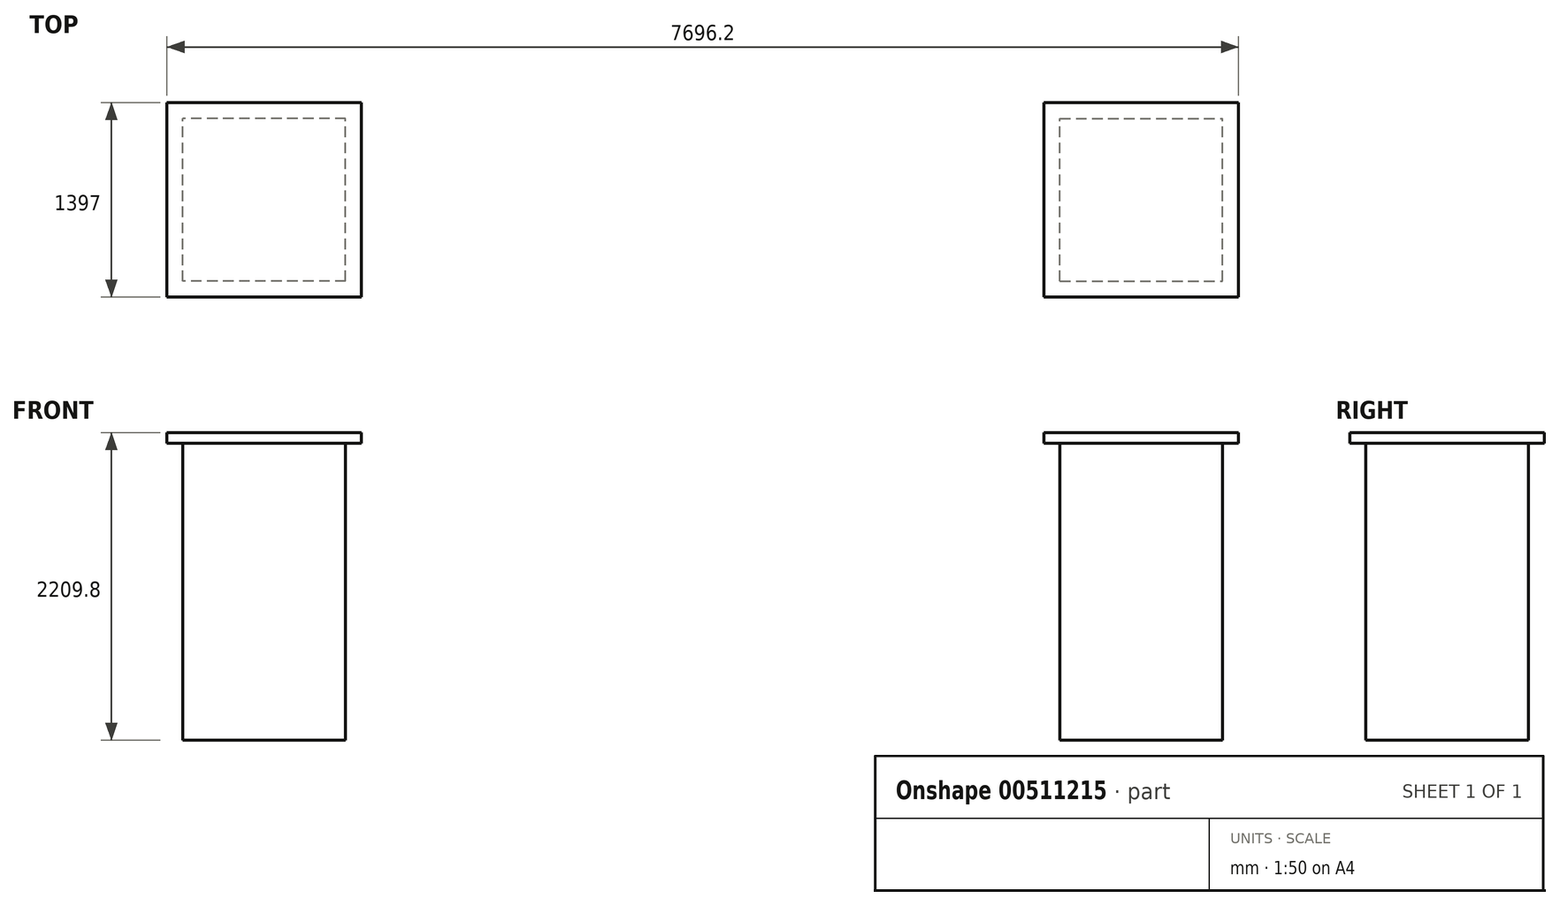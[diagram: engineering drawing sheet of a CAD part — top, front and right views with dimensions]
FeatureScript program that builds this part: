
annotation { "Feature Type Name" : "Feature", "Feature Type Description" : "" }
export const myFeature = defineFeature(function(context is Context, id is Id, definition is map)
    precondition{}
    {
        {
            var Q0;
            Q0=qCreatedBy(makeId("Top.planeOp"),FACE);
            var sketch = newSketch(context, id + "F0", { "sketchPlane" : qUnion([Q0])});
            skLineSegment(sketch, "E0.bottom", {"start": v(-2565.4, -584.2) * mm, "end": v(-3733.8, -584.2) * mm});
            skLineSegment(sketch, "E0.top", {"start": v(-2565.4, 584.2) * mm, "end": v(-3733.8, 584.2) * mm});
            skLineSegment(sketch, "E0.left", {"start": v(-2565.4, -584.2) * mm, "end": v(-2565.4, 584.2) * mm});
            skLineSegment(sketch, "E0.right", {"start": v(-3733.8, -584.2) * mm, "end": v(-3733.8, 584.2) * mm});
            skPoint(sketch, "E0.middle", {"position": v(-3149.6, 0) * mm});
            skLineSegment(sketch, "E1", {"start": v(-2565.4, 0) * mm, "end": v(2565.4, 0) * mm, "construction": true});
            skPoint(sketch, "E2", {"position": v(0, 0) * mm});
            skLineSegment(sketch, "E3", {"start": v(0, 0) * mm, "end": v(0, 584.2) * mm, "construction": true});
            skPoint(sketch, "E4.MirrorP", {"position": v(3149.6, 0) * mm});
            skLineSegment(sketch, "E5.MirrorCS", {"start": v(2565.4, -584.2) * mm, "end": v(3733.8, -584.2) * mm});
            skLineSegment(sketch, "E6.MirrorCS", {"start": v(2565.4, 584.2) * mm, "end": v(3733.8, 584.2) * mm});
            skLineSegment(sketch, "E7.MirrorCS", {"start": v(3733.8, -584.2) * mm, "end": v(3733.8, 584.2) * mm});
            skLineSegment(sketch, "E8.MirrorCS", {"start": v(2565.4, -584.2) * mm, "end": v(2565.4, 584.2) * mm});
            skLineSegment(sketch, "E9", {"start": v(-2362.2, 152.4) * mm, "end": v(-2362.2, -152.4) * mm, "construction": true});
            skLineSegment(sketch, "E10", {"start": v(2362.2, -152.4) * mm, "end": v(2362.2, 152.4) * mm, "construction": true});
            skPoint(sketch, "E11", {"position": v(-2362.2, 0) * mm});
            skPoint(sketch, "E12", {"position": v(2362.2, 0) * mm});
            skSolve(sketch);
        }
        {
            var Q0;
            Q0 = qSketchRegion(id + "F0", true);
            extrude(context, id + "F1", {"entities" : qUnion([Q0]), "flatOperationType" : FlatOperationType.REMOVE, "offsetDistance" : 25.4 * mm, "depth" : 2133.6 * mm, "domain" : OperationDomain.MODEL});
        }
        {
            var Q0;
            Q0=makeQuery(id+"F1.opExtrude","CAP_FACE",FACE,{"disambiguationData":[OSD([sQuery(id+"F0.wireOp",EDGE,"E0.bottom"),sQuery(id+"F0.wireOp",EDGE,"E0.top"),sQuery(id+"F0.wireOp",EDGE,"E0.left"),sQuery(id+"F0.wireOp",EDGE,"E0.right")])],"isStart":false});
            var sketch = newSketch(context, id + "F2", { "sketchPlane" : qUnion([Q0])});
            skLineSegment(sketch, "E13", {"start": v(-3149.6, -584.2) * mm, "end": v(-3149.6, 584.2) * mm, "construction": true});
            skLineSegment(sketch, "E14.bottom", {"start": v(-2451.1, -698.5) * mm, "end": v(-3848.1, -698.5) * mm});
            skLineSegment(sketch, "E14.top", {"start": v(-2451.1, 698.5) * mm, "end": v(-3848.1, 698.5) * mm});
            skLineSegment(sketch, "E14.left", {"start": v(-2451.1, -698.5) * mm, "end": v(-2451.1, 698.5) * mm});
            skLineSegment(sketch, "E14.right", {"start": v(-3848.1, -698.5) * mm, "end": v(-3848.1, 698.5) * mm});
            skPoint(sketch, "E14.middle", {"position": v(-3149.6, 0) * mm});
            skSolve(sketch);
        }
        {
            var Q0;
            Q0 = qSketchRegion(id + "F2", true);
            extrude(context, id + "F3", {"entities" : qUnion([Q0]), "flatOperationType" : FlatOperationType.REMOVE, "offsetDistance" : 25.4 * mm, "depth" : 76.2 * mm, "domain" : OperationDomain.MODEL});
        }
        {
            var Q0;
            Q0=makeQuery(id+"F3.opExtrude","SWEPT_BODY",BODY,{"disambiguationData":[OSD([sQuery(id+"F2.wireOp",EDGE,"E14.bottom"),sQuery(id+"F2.wireOp",EDGE,"E14.top"),sQuery(id+"F2.wireOp",EDGE,"E14.left"),sQuery(id+"F2.wireOp",EDGE,"E14.right")])]});
            var Q1;
            Q1=qCreatedBy(makeId("Right.planeOp"),FACE);
            mirror(context, id + "F4", {"entities" : qUnion([Q0]), "mirrorPlane" : qUnion([Q1])});
        }
    });
